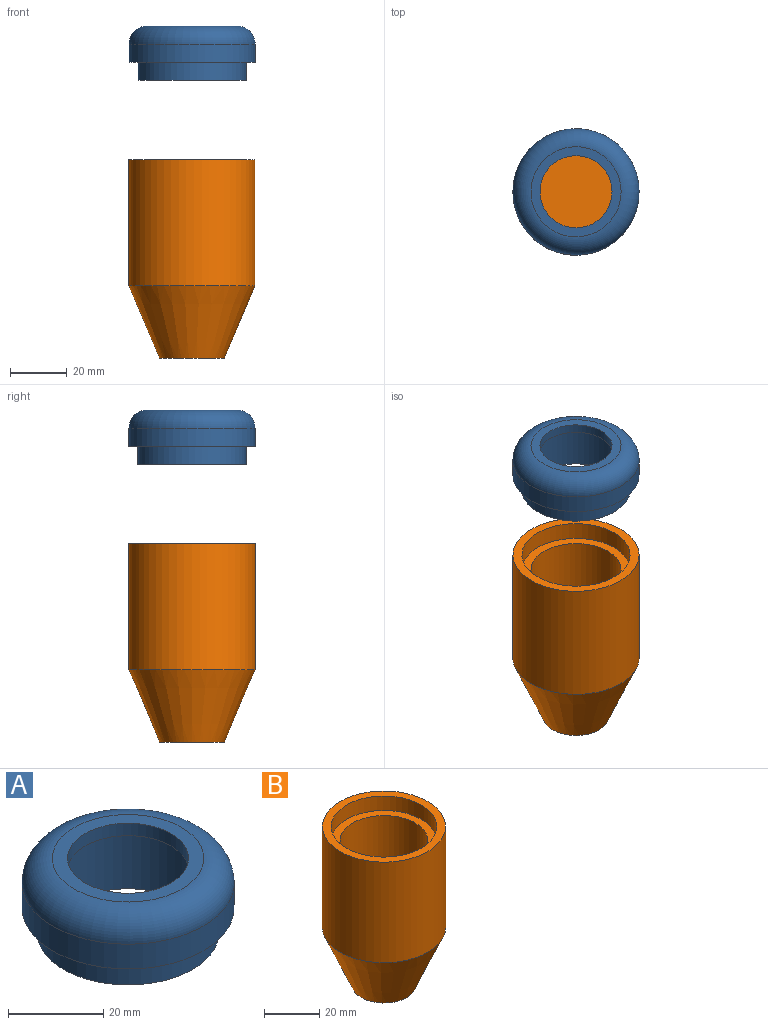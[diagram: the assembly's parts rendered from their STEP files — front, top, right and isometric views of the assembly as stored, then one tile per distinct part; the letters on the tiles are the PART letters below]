
ASSEMBLY  parts=2 mates=1
PART A: 9 faces, bbox 48.1x48.1x19 mm
  f0: plane 44.45x44.45mm, normal (0,0,-1), area 411.7mm2, adj f1,f8
  f1: cylinder r=22.23mm len=44.45mm, axis (0,0,1), area 886.7mm2, adj f0,f2
  f2: torus R=15.88mm, axis (0,0,1), area 1248.3mm2, adj f1,f3
  f3: plane 31.75x31.75mm, normal (0,0,1), area 285mm2, adj f2,f4
  f4: cylinder r=12.7mm len=25.4mm, axis (0,0,1), area 253.4mm2, adj f3,f5
  f5: plane 31.75x31.75mm, normal (0,0,-1), area 285mm2, adj f4,f6
  f6: cylinder r=15.88mm len=31.75mm, axis (0,0,1), area 1583.3mm2, adj f5,f7
  f7: plane 38.1x38.1mm, normal (0,0,-1), area 348.4mm2, adj f6,f8
  f8: cylinder r=19.05mm len=38.1mm, axis (0,0,1), area 759.9mm2, adj f0,f7
PART B: 10 faces, bbox 44.5x44.5x69.9 mm
  f0: cylinder r=15.88mm len=31.75mm, axis (0,0,-1), area 2913.6mm2, adj f1,f7
  f1: plane 38.1x38.1mm, normal (0,0,1), area 348.4mm2, adj f0,f2
  f2: cylinder r=19.05mm len=38.1mm, axis (0,0,-1), area 760.1mm2, adj f1,f3
  f3: plane 44.45x44.45mm, normal (0,0,1), area 411.7mm2, adj f2,f4
  f4: cylinder r=22.23mm len=44.45mm, axis (0,0,-1), area 6207.2mm2, adj f3,f5
  f5: cone r=22.23mm half-angle=23deg, axis (0,0,1), area 2918mm2, adj f4,f6
  f6: plane 22.86x22.86mm, normal (0,0,-1), area 317.2mm2, adj f5,f8
  f7: plane 31.75x31.75mm, normal (0,0,1), area 791.7mm2, adj f0
  f8: cylinder r=5.45mm len=25.4mm, axis (0,0,-1), area 869.5mm2, adj f6,f9
  f9: plane 10.9x10.9mm, normal (0,0,-1), area 93.3mm2, adj f8
PLACE A t=(-23.36,38.6,92.01)mm
PLACE B t=(-23.36,38.6,-12.22)mm
MATE slider B.f0 <-> A.f1  axis (0,0,-1) through (-23.36,38.6,54.45)mm
